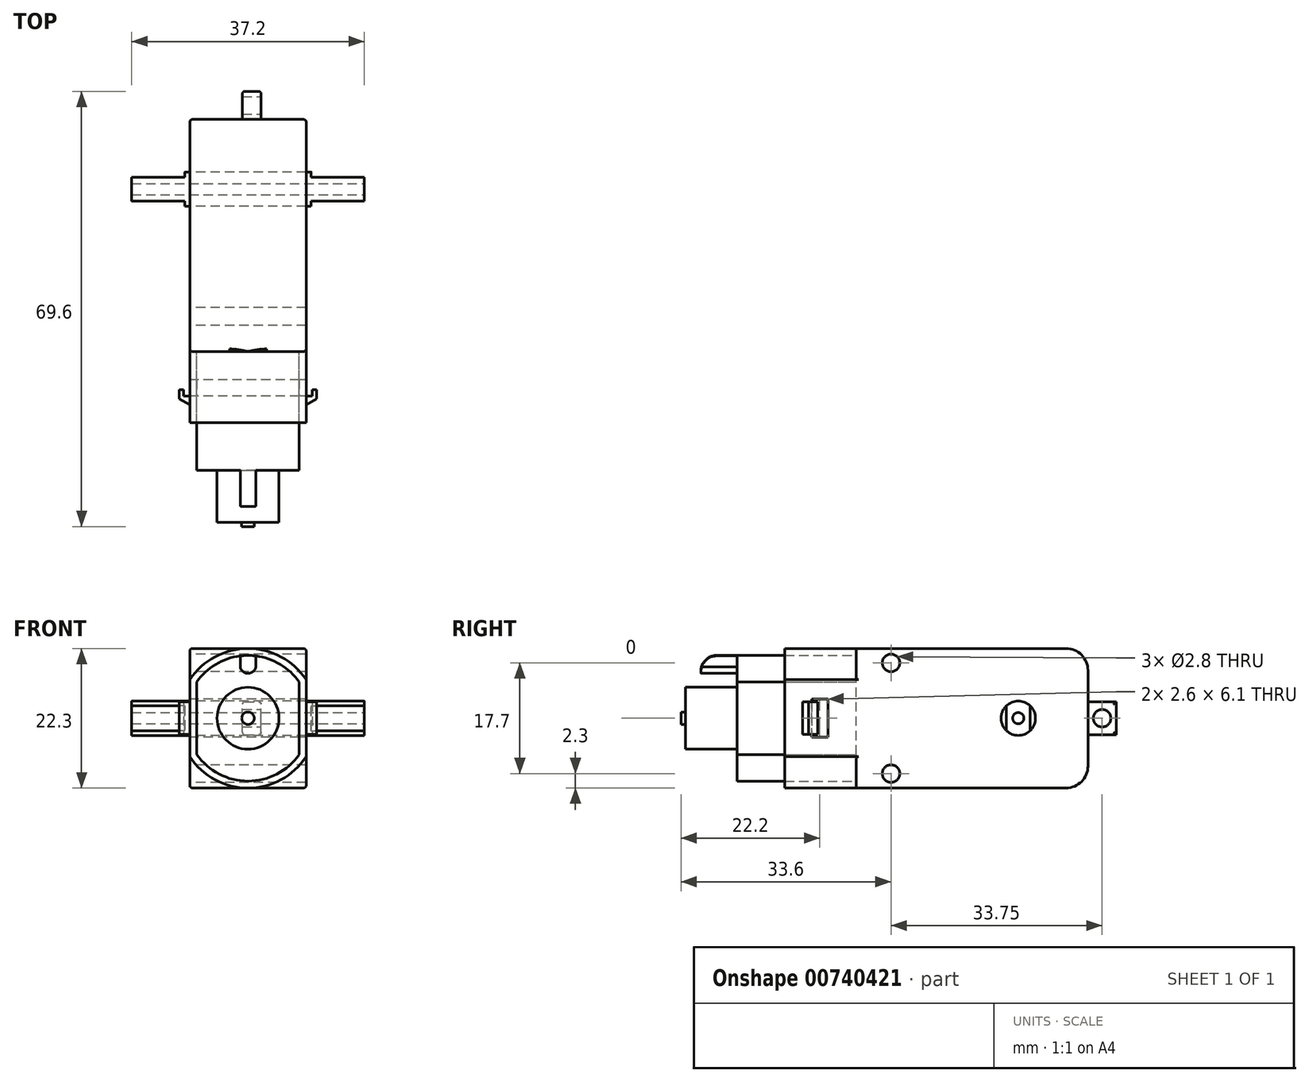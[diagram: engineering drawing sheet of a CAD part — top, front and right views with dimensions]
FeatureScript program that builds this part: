
annotation { "Feature Type Name" : "Feature", "Feature Type Description" : "" }
export const myFeature = defineFeature(function(context is Context, id is Id, definition is map)
    precondition{}
    {
        {
            var Q0;
            Q0=qCreatedBy(makeId("Front.planeOp"),FACE);
            var sketch = newSketch(context, id + "F0", { "sketchPlane" : qUnion([Q0])});
            skLineSegment(sketch, "E0.bottom", {"start": v(9.3, -11.15) * mm, "end": v(-9.3, -11.15) * mm});
            skLineSegment(sketch, "E0.top", {"start": v(9.3, 11.15) * mm, "end": v(-9.3, 11.15) * mm});
            skLineSegment(sketch, "E0.left", {"start": v(9.3, -11.15) * mm, "end": v(9.3, 11.15) * mm});
            skLineSegment(sketch, "E0.right", {"start": v(-9.3, -11.15) * mm, "end": v(-9.3, 11.15) * mm});
            skPoint(sketch, "E0.middle", {"position": v(0, 0) * mm});
            skSolve(sketch);
        }
        {
            var Q0;
            Q0=qSketchRegion(id+"F0",true);
            extrude(context, id + "F1", {"entities" : qUnion([Q0]), "depth" : 37.1 * mm});
        }
        {
            var Q0;
            Q0=makeQuery(id+"F1.opExtrude","SWEPT_FACE",FACE,{"disambiguationData":[OSD([sQuery(id+"F0.wireOp",EDGE,"E0.right")])]});
            var sketch = newSketch(context, id + "F2", { "sketchPlane" : qUnion([Q0])});
            skCircle(sketch, "E1", {"center": v(31.5, -8.85) * mm, "radius": 1.4 * mm});
            skLineSegment(sketch, "E2", {"start": v(0, 0) * mm, "end": v(37.1, 0) * mm, "construction": true});
            skCircle(sketch, "E3.MirrorC", {"center": v(31.5, 8.85) * mm, "radius": 1.4 * mm});
            skCircle(sketch, "E4", {"center": v(11.15, 0) * mm, "radius": 2.75 * mm});
            skSolve(sketch);
        }
        {
            var Q0;
            Q0=makeQuery(id+"F1.opExtrude","CAP_FACE",FACE,{"disambiguationData":[OSD([sQuery(id+"F0.wireOp",EDGE,"E0.bottom"),sQuery(id+"F0.wireOp",EDGE,"E0.top"),sQuery(id+"F0.wireOp",EDGE,"E0.left"),sQuery(id+"F0.wireOp",EDGE,"E0.right")])],"isStart":false});
            var sketch = newSketch(context, id + "F3", { "sketchPlane" : qUnion([Q0])});
            skArc(sketch, "E5", {"start": v(-9.3, -6.15) * mm, "mid": v(0, -11.15) * mm, "end": v(9.3, -6.15) * mm});
            skLineSegment(sketch, "E6.0", {"start": v(9.3, -6.15) * mm, "end": v(9.3, 6.15) * mm});
            skLineSegment(sketch, "E6.1", {"start": v(-9.3, -6.15) * mm, "end": v(-9.3, 6.15) * mm});
            skArc(sketch, "E7.trimOffspring", {"start": v(9.3, 6.15) * mm, "mid": v(0, 11.15) * mm, "end": v(-9.3, 6.15) * mm});
            skPoint(sketch, "E8.orphan", {"position": v(-9.3, 11.15) * mm});
            skPoint(sketch, "E9.orphan", {"position": v(9.3, 11.15) * mm});
            skPoint(sketch, "E10.orphan", {"position": v(9.3, -11.15) * mm});
            skPoint(sketch, "E11.orphan", {"position": v(-9.3, -11.15) * mm});
            skArc(sketch, "E12.0", {"start": v(8.2, 5.81) * mm, "mid": v(0, 10.05) * mm, "end": v(-8.2, 5.81) * mm});
            skLineSegment(sketch, "E12.1", {"start": v(8.2, -5.81) * mm, "end": v(8.2, 5.81) * mm});
            skArc(sketch, "E12.2", {"start": v(-8.2, -5.81) * mm, "mid": v(0, -10.05) * mm, "end": v(8.2, -5.81) * mm});
            skLineSegment(sketch, "E12.3", {"start": v(-8.2, -5.81) * mm, "end": v(-8.2, 5.81) * mm});
            skSolve(sketch);
        }
        {
            var Q0;
            Q0=qSketchRegion(id+"F3",true);
            extrude(context, id + "F4", {"entities" : qUnion([Q0]), "operationType" : NewBodyOperationType.ADD, "depth" : 11.4 * mm});
        }
        {
            var Q0;
            {var subQ0=sQuery(id+"F0.wireOp",EDGE,"F8vdl7xD-wS4J-gisc-z2d9-TpghqO1zXRkm");Q0=makeQuery(id+"F4.boolean.opBoolean","SPLIT",FACE,{"disambiguationData":[TD([makeQuery(id+"F1.opExtrude","SWEPT_FACE",FACE,{"disambiguationData":[OSD([subQ0])]}),makeQuery(id+"F4.opExtrude","SWEPT_FACE",FACE,{"disambiguationData":[OSD([sQuery(id+"F3.wireOp",EDGE,"E12.0")])]}),makeQuery(id+"F4.opExtrude","SWEPT_FACE",FACE,{"disambiguationData":[OSD([sQuery(id+"F3.wireOp",EDGE,"E12.1")])]}),makeQuery(id+"F4.opExtrude","SWEPT_FACE",FACE,{"disambiguationData":[OSD([sQuery(id+"F3.wireOp",EDGE,"E12.2")])]}),makeQuery(id+"F4.opExtrude","SWEPT_FACE",FACE,{"disambiguationData":[OSD([sQuery(id+"F3.wireOp",EDGE,"E12.3")])]})])],"derivedFrom":makeQuery(id+"F1.opExtrude","CAP_FACE",FACE,{"disambiguationData":[OSD([sQuery(id+"F0.wireOp",EDGE,"E0.bottom"),sQuery(id+"F0.wireOp",EDGE,"E0.top"),sQuery(id+"F0.wireOp",EDGE,"E0.left"),sQuery(id+"F0.wireOp",EDGE,"E0.right"),subQ0])],"isStart":false})});}
            var sketch = newSketch(context, id + "F5", { "sketchPlane" : qUnion([Q0])});
            skLineSegment(sketch, "E13.0", {"start": v(-8.2, -5.81) * mm, "end": v(-8.2, 5.81) * mm});
            skArc(sketch, "E13.1", {"start": v(8.2, 5.81) * mm, "mid": v(0, 10.05) * mm, "end": v(-8.2, 5.81) * mm});
            skLineSegment(sketch, "E13.2", {"start": v(8.2, -5.81) * mm, "end": v(8.2, 5.81) * mm});
            skArc(sketch, "E13.3", {"start": v(-8.2, -5.81) * mm, "mid": v(0, -10.05) * mm, "end": v(8.2, -5.81) * mm});
            skSolve(sketch);
        }
        {
            var Q0;
            Q0=qSketchRegion(id+"F5",true);
            extrude(context, id + "F6", {"entities" : qUnion([Q0]), "depth" : 24.8 * mm});
        }
        {
            var Q0;
            Q0=qSketchRegion(id+"F2",true);
            extrude(context, id + "F7", {"entities" : qUnion([Q0]), "operationType" : NewBodyOperationType.REMOVE, "oppositeDirection" : true, "depth" : 25 * mm});
        }
        {
            var Q0;
            Q0=qCreatedBy(makeId("Right.planeOp"),FACE);
            var sketch = newSketch(context, id + "F8", { "sketchPlane" : qUnion([Q0])});
            skCircle(sketch, "E14", {"center": v(-11.15, 0) * mm, "radius": 2.75 * mm});
            skSolve(sketch);
        }
        {
            var Q0;
            Q0=qSketchRegion(id+"F8",true);
            extrude(context, id + "F9", {"entities" : qUnion([Q0]), "endBound" : BoundingType.SYMMETRIC, "depth" : 37.2 * mm});
        }
        {
            var Q0;
            Q0=makeQuery(id+"F9.opExtrude","CAP_FACE",FACE,{"disambiguationData":[OSD([sQuery(id+"F8.wireOp",EDGE,"E14")])],"isStart":false});
            var sketch = newSketch(context, id + "F10", { "sketchPlane" : qUnion([Q0])});
            skLineSegment(sketch, "E15", {"start": v(-9.25, -1.99) * mm, "end": v(-9.25, 1.99) * mm});
            skLineSegment(sketch, "E16", {"start": v(-13.05, -1.99) * mm, "end": v(-13.05, 1.99) * mm});
            skPoint(sketch, "E17.start.orphan", {"position": v(-8.4, 0) * mm});
            skArc(sketch, "E18.0", {"start": v(-9.25, -1.99) * mm, "mid": v(-8.4, 0) * mm, "end": v(-9.25, 1.99) * mm});
            skArc(sketch, "E19.trimOffspring", {"start": v(-13.05, 1.99) * mm, "mid": v(-13.9, 0) * mm, "end": v(-13.05, -1.99) * mm});
            skSolve(sketch);
        }
        {
            var Q0;
            Q0=qSketchRegion(id+"F10",true);
            extrude(context, id + "F11", {"entities" : qUnion([Q0]), "operationType" : NewBodyOperationType.REMOVE, "oppositeDirection" : true, "depth" : 8.5 * mm});
        }
        {
            var Q0;
            Q0=makeQuery(id+"F9.opExtrude","CAP_FACE",FACE,{"disambiguationData":[OSD([sQuery(id+"F8.wireOp",EDGE,"E14")])],"isStart":true});
            var sketch = newSketch(context, id + "F12", { "sketchPlane" : qUnion([Q0])});
            skLineSegment(sketch, "E20", {"start": v(9.25, 1.99) * mm, "end": v(9.25, -1.99) * mm});
            skLineSegment(sketch, "E21", {"start": v(13.05, 1.99) * mm, "end": v(13.05, -1.99) * mm});
            skPoint(sketch, "E22.start.orphan", {"position": v(9.25, 0) * mm});
            skPoint(sketch, "E23.start.orphan", {"position": v(13.05, 0) * mm});
            skArc(sketch, "E24.0", {"start": v(9.25, 1.99) * mm, "mid": v(11.15, -2.75) * mm, "end": v(13.05, 1.99) * mm});
            skSolve(sketch);
        }
        {
            var Q0;
            Q0=qSketchRegion(id+"F12",true);
            extrude(context, id + "F13", {"entities" : qUnion([Q0]), "operationType" : NewBodyOperationType.REMOVE, "oppositeDirection" : true, "depth" : 8.5 * mm});
        }
        {
            var Q0;
            Q0=makeQuery(id+"F1.opExtrude","CAP_FACE",FACE,{"disambiguationData":[OSD([sQuery(id+"F0.wireOp",EDGE,"E0.bottom"),sQuery(id+"F0.wireOp",EDGE,"E0.top"),sQuery(id+"F0.wireOp",EDGE,"E0.left"),sQuery(id+"F0.wireOp",EDGE,"E0.right")])],"isStart":true});
            var sketch = newSketch(context, id + "F14", { "sketchPlane" : qUnion([Q0])});
            skPoint(sketch, "E25.middle", {"position": v(-0.6, 0) * mm});
            skLineSegment(sketch, "E26.bottom", {"start": v(0.9, -2.63) * mm, "end": v(-2.1, -2.63) * mm});
            skLineSegment(sketch, "E26.top", {"start": v(0.9, 2.63) * mm, "end": v(-2.1, 2.63) * mm});
            skLineSegment(sketch, "E26.left", {"start": v(0.9, -2.63) * mm, "end": v(0.9, 2.63) * mm});
            skLineSegment(sketch, "E26.right", {"start": v(-2.1, -2.63) * mm, "end": v(-2.1, 2.63) * mm});
            skSolve(sketch);
        }
        {
            var Q0;
            Q0=qSketchRegion(id+"F14",true);
            extrude(context, id + "F15", {"entities" : qUnion([Q0]), "operationType" : NewBodyOperationType.ADD, "depth" : 4.5 * mm});
        }
        {
            var Q0;
            Q0=makeQuery(id+"F4.boolean.opBoolean","MERGE",FACE,{"derivedFrom":[makeQuery(id+"F1.opExtrude","SWEPT_FACE",FACE,{"disambiguationData":[OSD([sQuery(id+"F0.wireOp",EDGE,"E0.right")])]}),makeQuery(id+"F4.opExtrude","SWEPT_FACE",FACE,{"disambiguationData":[OSD([sQuery(id+"F3.wireOp",EDGE,"E6.1")])]})]});
            var sketch = newSketch(context, id + "F16", { "sketchPlane" : qUnion([Q0])});
            skLineSegment(sketch, "E27.bottom", {"start": v(41.6, -3.05) * mm, "end": v(44.2, -3.05) * mm});
            skLineSegment(sketch, "E27.top", {"start": v(41.6, 3.05) * mm, "end": v(44.2, 3.05) * mm});
            skLineSegment(sketch, "E27.left", {"start": v(41.6, -3.05) * mm, "end": v(41.6, 3.05) * mm});
            skLineSegment(sketch, "E27.right", {"start": v(44.2, -3.05) * mm, "end": v(44.2, 3.05) * mm});
            skPoint(sketch, "E27.middle", {"position": v(42.9, 0) * mm});
            skSolve(sketch);
        }
        {
            var Q0;
            Q0=makeQuery(id+"F6.opExtrude","CAP_FACE",FACE,{"disambiguationData":[OSD([sQuery(id+"F5.wireOp",EDGE,"E13.0"),sQuery(id+"F5.wireOp",EDGE,"E13.1"),sQuery(id+"F5.wireOp",EDGE,"E13.2"),sQuery(id+"F5.wireOp",EDGE,"E13.3")])],"isStart":false});
            var sketch = newSketch(context, id + "F17", { "sketchPlane" : qUnion([Q0])});
            skCircle(sketch, "E28", {"center": v(0, 0) * mm, "radius": 4.95 * mm});
            skCircle(sketch, "E29", {"center": v(0, 0) * mm, "radius": 1 * mm});
            skSolve(sketch);
        }
        {
            var Q0;
            Q0=makeQuery(id+"F17.imprint","IMPRINT",FACE,{"disambiguationData":[TD([[makeQuery(id+"F17.imprint","IMPRINT",EDGE,{"derivedFrom":sQuery(id+"F17.wireOp",EDGE,"E29")}),1.0]])]});
            extrude(context, id + "F18", {"entities" : qUnion([Q0]), "operationType" : NewBodyOperationType.ADD, "depth" : 3.2 * mm});
        }
        {
            var Q0;
            Q0=makeQuery(id+"F17.imprint","IMPRINT",FACE,{"disambiguationData":[TD([[makeQuery(id+"F17.imprint","IMPRINT",EDGE,{"derivedFrom":sQuery(id+"F17.wireOp",EDGE,"E28")}),1.0]])]});
            extrude(context, id + "F19", {"entities" : qUnion([Q0]), "operationType" : NewBodyOperationType.ADD, "depth" : 2.5 * mm});
        }
        {
            var Q0;
            Q0=makeQuery(id+"F17.imprint","IMPRINT",FACE,{"disambiguationData":[TD([[makeQuery(id+"F17.imprint","IMPRINT",EDGE,{"derivedFrom":sQuery(id+"F17.wireOp",EDGE,"E28")}),-1.0]])]});
            var sketch = newSketch(context, id + "F20", { "sketchPlane" : qUnion([Q0])});
            skArc(sketch, "E30.0", {"start": v(-1.25, -9.97) * mm, "mid": v(0, -10.05) * mm, "end": v(1.25, -9.97) * mm});
            skLineSegment(sketch, "E31", {"start": v(-1.25, -9.97) * mm, "end": v(-1.25, -8.18) * mm});
            skLineSegment(sketch, "E32", {"start": v(1.25, -9.97) * mm, "end": v(1.25, -8.18) * mm});
            skArc(sketch, "E33", {"start": v(1.25, -8.18) * mm, "mid": v(0, -7.18) * mm, "end": v(-1.25, -8.18) * mm});
            skArc(sketch, "E34.MirrorCS", {"start": v(1.25, 8.18) * mm, "mid": v(0, 7.18) * mm, "end": v(-1.25, 8.18) * mm});
            skLineSegment(sketch, "E35.MirrorCS", {"start": v(1.25, 9.97) * mm, "end": v(1.25, 8.18) * mm});
            skLineSegment(sketch, "E36.MirrorCS", {"start": v(-1.25, 9.97) * mm, "end": v(-1.25, 8.18) * mm});
            skArc(sketch, "E37.0", {"start": v(1.25, 9.97) * mm, "mid": v(0, 10.05) * mm, "end": v(-1.25, 9.97) * mm});
            skPoint(sketch, "E38.orphan", {"position": v(-8.2, 5.81) * mm});
            skPoint(sketch, "E39.orphan", {"position": v(8.2, 5.81) * mm});
            skPoint(sketch, "E40.orphan", {"position": v(8.2, -5.81) * mm});
            skPoint(sketch, "E41.orphan", {"position": v(-8.2, -5.81) * mm});
            skSolve(sketch);
        }
        {
            var Q0;
            Q0=makeQuery(id+"F16.imprint","IMPRINT",FACE,{"disambiguationData":[TD([[makeQuery(id+"F16.imprint","IMPRINT",EDGE,{"derivedFrom":sQuery(id+"F16.wireOp",EDGE,"E27.bottom")}),1.0]])]});
            extrude(context, id + "F21", {"entities" : qUnion([Q0]), "operationType" : NewBodyOperationType.REMOVE, "oppositeDirection" : true, "depth" : 25 * mm});
        }
        {
            var Q0;
            Q0=qCreatedBy(makeId("Top.planeOp"),FACE);
            var sketch = newSketch(context, id + "F22", { "sketchPlane" : qUnion([Q0])});
            skPoint(sketch, "E42.0", {"position": v(-9.3, -44.2) * mm});
            skLineSegment(sketch, "E43", {"start": v(-9.3, -44.2) * mm, "end": v(-9.3, -45.65) * mm});
            skLineSegment(sketch, "E44", {"start": v(-9.3, -45.65) * mm, "end": v(-11, -44.7) * mm});
            skLineSegment(sketch, "E45", {"start": v(-11, -44.7) * mm, "end": v(-11, -43.2) * mm});
            skLineSegment(sketch, "E46", {"start": v(-11, -43.2) * mm, "end": v(-10.3, -43.2) * mm});
            skLineSegment(sketch, "E47", {"start": v(-10.3, -43.2) * mm, "end": v(-10.3, -44.2) * mm});
            skLineSegment(sketch, "E48", {"start": v(-10.3, -44.2) * mm, "end": v(-9.3, -44.2) * mm});
            skSolve(sketch);
        }
        {
            var Q0;
            Q0=makeQuery(id+"F22.imprint","IMPRINT",FACE,{"disambiguationData":[TD([[makeQuery(id+"F22.imprint","IMPRINT",EDGE,{"derivedFrom":sQuery(id+"F22.wireOp",EDGE,"E43")}),-1.0]])]});
            extrude(context, id + "F23", {"entities" : qUnion([Q0]), "operationType" : NewBodyOperationType.ADD, "endBound" : BoundingType.SYMMETRIC, "depth" : 5.2 * mm});
        }
        {
            var Q0;
            Q0=makeQuery(id+"F9.opExtrude","CAP_FACE",FACE,{"disambiguationData":[OSD([sQuery(id+"F8.wireOp",EDGE,"E14")])],"isStart":false});
            var sketch = newSketch(context, id + "F24", { "sketchPlane" : qUnion([Q0])});
            skCircle(sketch, "E49", {"center": v(-11.15, 0) * mm, "radius": 0.9 * mm});
            skSolve(sketch);
        }
        {
            var Q0;
            Q0=qSketchRegion(id+"F24",true);
            extrude(context, id + "F25", {"entities" : qUnion([Q0]), "operationType" : NewBodyOperationType.REMOVE, "endBound" : BoundingType.THROUGH_ALL, "oppositeDirection" : true, "depth" : 25 * mm});
        }
        {
            var Q0;
            Q0=qCreatedBy(makeId("Top.planeOp"),FACE);
            var sketch = newSketch(context, id + "F26", { "sketchPlane" : qUnion([Q0])});
            skPoint(sketch, "E50.0", {"position": v(9.3, -44.2) * mm});
            skLineSegment(sketch, "E51", {"start": v(9.3, -44.2) * mm, "end": v(9.3, -45.65) * mm});
            skLineSegment(sketch, "E52", {"start": v(9.3, -45.65) * mm, "end": v(11, -44.7) * mm});
            skLineSegment(sketch, "E53", {"start": v(11, -44.7) * mm, "end": v(11, -43.2) * mm});
            skLineSegment(sketch, "E54", {"start": v(11, -43.2) * mm, "end": v(10.3, -43.2) * mm});
            skLineSegment(sketch, "E55", {"start": v(10.3, -43.2) * mm, "end": v(10.3, -44.2) * mm});
            skLineSegment(sketch, "E56", {"start": v(10.3, -44.2) * mm, "end": v(9.3, -44.2) * mm});
            skSolve(sketch);
        }
        {
            var Q0;
            Q0=makeQuery(id+"F26.imprint","IMPRINT",FACE,{"disambiguationData":[TD([[makeQuery(id+"F26.imprint","IMPRINT",EDGE,{"derivedFrom":sQuery(id+"F26.wireOp",EDGE,"E51")}),1.0]])]});
            extrude(context, id + "F27", {"entities" : qUnion([Q0]), "operationType" : NewBodyOperationType.ADD, "endBound" : BoundingType.SYMMETRIC, "depth" : 5.2 * mm});
        }
        {
            var Q0;
            Q0=makeQuery(id+"F20.imprint","IMPRINT",FACE,{"disambiguationData":[TD([[makeQuery(id+"F20.imprint","IMPRINT",EDGE,{"derivedFrom":sQuery(id+"F20.wireOp",EDGE,"E34.MirrorCS")}),-1.0]])]});
            var Q1;
            Q1=makeQuery(id+"F20.imprint","IMPRINT",FACE,{"disambiguationData":[TD([[makeQuery(id+"F20.imprint","IMPRINT",EDGE,{"derivedFrom":sQuery(id+"F20.wireOp",EDGE,"E30.0")}),1.0]])]});
            extrude(context, id + "F28", {"entities" : qUnion([Q0, Q1]), "operationType" : NewBodyOperationType.REMOVE, "oppositeDirection" : true, "depth" : 5.8 * mm});
        }
        {
            var Q0;
            Q0=makeQuery(id+"F15.opExtrude","SWEPT_FACE",FACE,{"disambiguationData":[OSD([sQuery(id+"F14.wireOp",EDGE,"E26.right")])]});
            var sketch = newSketch(context, id + "F29", { "sketchPlane" : qUnion([Q0])});
            skPoint(sketch, "E57.end.orphan", {"position": v(-4.5, 0) * mm});
            skPoint(sketch, "E57.start.orphan", {"position": v(-3.65, 0) * mm});
            skPoint(sketch, "E58.start.orphan", {"position": v(-0.85, 0) * mm});
            skCircle(sketch, "E59", {"center": v(2.25, 0) * mm, "radius": 1.4 * mm});
            skLineSegment(sketch, "E60", {"start": v(2.25, 2.63) * mm, "end": v(2.25, 0) * mm, "construction": true});
            skLineSegment(sketch, "E61", {"start": v(4.5, 0) * mm, "end": v(2.25, 0) * mm, "construction": true});
            skSolve(sketch);
        }
        {
            var Q0;
            Q0=makeQuery(id+"F29.imprint","IMPRINT",FACE,{"disambiguationData":[TD([[makeQuery(id+"F29.imprint","IMPRINT",EDGE,{"derivedFrom":sQuery(id+"F29.wireOp",EDGE,"E59")}),1.0]])]});
            extrude(context, id + "F30", {"entities" : qUnion([Q0]), "operationType" : NewBodyOperationType.REMOVE, "endBound" : BoundingType.THROUGH_ALL, "oppositeDirection" : true, "depth" : 25 * mm, "offsetDistance" : 25 * mm});
        }
        {
            var Q0;
            Q0=makeQuery(id+"F1.opExtrude","CAP_EDGE",EDGE,{"disambiguationData":[OSD([sQuery(id+"F0.wireOp",EDGE,"E0.top")])],"isStart":true});
            var Q1;
            Q1=makeQuery(id+"F1.opExtrude","CAP_EDGE",EDGE,{"disambiguationData":[OSD([sQuery(id+"F0.wireOp",EDGE,"E0.bottom")])],"isStart":true});
            fillet(context, id + "F31", {"entities" : qUnion([Q0, Q1]), "radius" : 3.5 * mm, "tangentPropagation" : true, "allowEdgeOverflow" : false});
        }
        {
            var Q0;
            {var subQ0=sQuery(id+"F0.wireOp",EDGE,"E0.right");var subQ1=sQuery(id+"F0.wireOp",EDGE,"E0.top");Q0=makeQuery(id+"F4.boolean.opBoolean","SPLIT",EDGE,{"disambiguationData":[TD([makeQuery(id+"F1.opExtrude","SWEPT_FACE",FACE,{"disambiguationData":[OSD([subQ0])]})])],"derivedFrom":makeQuery(id+"F1.opExtrude","CAP_EDGE",EDGE,{"disambiguationData":[OSD([subQ1])],"isStart":false})});}
            var Q1;
            {var subQ0=sQuery(id+"F0.wireOp",EDGE,"E0.left");var subQ1=sQuery(id+"F0.wireOp",EDGE,"E0.top");Q1=makeQuery(id+"F4.boolean.opBoolean","SPLIT",EDGE,{"disambiguationData":[TD([makeQuery(id+"F1.opExtrude","SWEPT_FACE",FACE,{"disambiguationData":[OSD([subQ0])]})])],"derivedFrom":makeQuery(id+"F1.opExtrude","CAP_EDGE",EDGE,{"disambiguationData":[OSD([subQ1])],"isStart":false})});}
            var Q2;
            {var subQ0=sQuery(id+"F0.wireOp",EDGE,"E0.left");var subQ1=sQuery(id+"F0.wireOp",EDGE,"E0.bottom");Q2=makeQuery(id+"F4.boolean.opBoolean","SPLIT",EDGE,{"disambiguationData":[TD([makeQuery(id+"F1.opExtrude","SWEPT_FACE",FACE,{"disambiguationData":[OSD([subQ0])]})])],"derivedFrom":makeQuery(id+"F1.opExtrude","CAP_EDGE",EDGE,{"disambiguationData":[OSD([subQ1])],"isStart":false})});}
            var Q3;
            {var subQ0=sQuery(id+"F0.wireOp",EDGE,"E0.right");var subQ1=sQuery(id+"F0.wireOp",EDGE,"E0.bottom");Q3=makeQuery(id+"F4.boolean.opBoolean","SPLIT",EDGE,{"disambiguationData":[TD([makeQuery(id+"F1.opExtrude","SWEPT_FACE",FACE,{"disambiguationData":[OSD([subQ0])]})])],"derivedFrom":makeQuery(id+"F1.opExtrude","CAP_EDGE",EDGE,{"disambiguationData":[OSD([subQ1])],"isStart":false})});}
            var Q4;
            {var subQ0=sQuery(id+"F0.wireOp",EDGE,"E0.right");var subQ1=sQuery(id+"F0.wireOp",EDGE,"E0.bottom");Q4=makeQuery(id+"F4.boolean.opBoolean","SPLIT",EDGE,{"disambiguationData":[TD([makeQuery(id+"F1.opExtrude","SWEPT_FACE",FACE,{"disambiguationData":[OSD([subQ1])]})])],"derivedFrom":makeQuery(id+"F1.opExtrude","CAP_EDGE",EDGE,{"disambiguationData":[OSD([subQ0])],"isStart":false})});}
            var Q5;
            {var subQ0=sQuery(id+"F0.wireOp",EDGE,"E0.left");var subQ1=sQuery(id+"F0.wireOp",EDGE,"E0.bottom");Q5=makeQuery(id+"F4.boolean.opBoolean","SPLIT",EDGE,{"disambiguationData":[TD([makeQuery(id+"F1.opExtrude","SWEPT_FACE",FACE,{"disambiguationData":[OSD([subQ1])]})])],"derivedFrom":makeQuery(id+"F1.opExtrude","CAP_EDGE",EDGE,{"disambiguationData":[OSD([subQ0])],"isStart":false})});}
            var Q6;
            {var subQ0=sQuery(id+"F0.wireOp",EDGE,"E0.left");var subQ1=sQuery(id+"F0.wireOp",EDGE,"E0.top");Q6=makeQuery(id+"F4.boolean.opBoolean","SPLIT",EDGE,{"disambiguationData":[TD([makeQuery(id+"F1.opExtrude","SWEPT_FACE",FACE,{"disambiguationData":[OSD([subQ1])]})])],"derivedFrom":makeQuery(id+"F1.opExtrude","CAP_EDGE",EDGE,{"disambiguationData":[OSD([subQ0])],"isStart":false})});}
            var Q7;
            {var subQ0=sQuery(id+"F0.wireOp",EDGE,"E0.right");var subQ1=sQuery(id+"F0.wireOp",EDGE,"E0.top");Q7=makeQuery(id+"F4.boolean.opBoolean","SPLIT",EDGE,{"disambiguationData":[TD([makeQuery(id+"F1.opExtrude","SWEPT_FACE",FACE,{"disambiguationData":[OSD([subQ1])]})])],"derivedFrom":makeQuery(id+"F1.opExtrude","CAP_EDGE",EDGE,{"disambiguationData":[OSD([subQ0])],"isStart":false})});}
            var Q8;
            Q8=makeQuery(id+"F1.opExtrude","SWEPT_EDGE",EDGE,{"disambiguationData":[OSD([sQuery(id+"F0.wireOp",EDGE,"E0.top"),sQuery(id+"F0.wireOp",EDGE,"E0.right")])]});
            var Q9;
            Q9=makeQuery(id+"F1.opExtrude","SWEPT_EDGE",EDGE,{"disambiguationData":[OSD([sQuery(id+"F0.wireOp",EDGE,"E0.bottom"),sQuery(id+"F0.wireOp",EDGE,"E0.left")])]});
            var Q10;
            Q10=makeQuery(id+"F15.opExtrude","SWEPT_EDGE",EDGE,{"disambiguationData":[OSD([sQuery(id+"F14.wireOp",EDGE,"E26.top"),sQuery(id+"F14.wireOp",EDGE,"E26.right")])]});
            var Q11;
            Q11=makeQuery(id+"F15.opExtrude","CAP_EDGE",EDGE,{"disambiguationData":[OSD([sQuery(id+"F14.wireOp",EDGE,"E26.right")])],"isStart":false});
            var Q12;
            Q12=makeQuery(id+"F15.opExtrude","SWEPT_EDGE",EDGE,{"disambiguationData":[OSD([sQuery(id+"F14.wireOp",EDGE,"E26.bottom"),sQuery(id+"F14.wireOp",EDGE,"E26.right")])]});
            var Q13;
            Q13=makeQuery(id+"F15.opExtrude","SWEPT_EDGE",EDGE,{"disambiguationData":[OSD([sQuery(id+"F14.wireOp",EDGE,"E26.top"),sQuery(id+"F14.wireOp",EDGE,"E26.left")])]});
            var Q14;
            Q14=makeQuery(id+"F15.opExtrude","CAP_EDGE",EDGE,{"disambiguationData":[OSD([sQuery(id+"F14.wireOp",EDGE,"E26.left")])],"isStart":false});
            var Q15;
            Q15=makeQuery(id+"F15.opExtrude","SWEPT_EDGE",EDGE,{"disambiguationData":[OSD([sQuery(id+"F14.wireOp",EDGE,"E26.bottom"),sQuery(id+"F14.wireOp",EDGE,"E26.left")])]});
            fillet(context, id + "F32", {"entities" : qUnion([Q0, Q1, Q2, Q3, Q4, Q5, Q6, Q7, Q8, Q9, Q10, Q11, Q12, Q13, Q14, Q15]), "radius" : .4 * mm, "tangentPropagation" : true, "allowEdgeOverflow" : false});
        }
        {
            var Q0;
            {var subQ0=sQuery(id+"F5.wireOp",EDGE,"E13.0");var subQ1=sQuery(id+"F5.wireOp",EDGE,"E13.1");Q0=makeQuery(id+"F28.boolean.opBoolean","SPLIT",EDGE,{"disambiguationData":[TD([makeQuery(id+"F6.opExtrude","SWEPT_FACE",FACE,{"disambiguationData":[OSD([subQ0])]})])],"derivedFrom":makeQuery(id+"F6.opExtrude","CAP_EDGE",EDGE,{"disambiguationData":[OSD([subQ1])],"isStart":false})});}
            var Q1;
            {var subQ0=sQuery(id+"F5.wireOp",EDGE,"E13.0");var subQ1=sQuery(id+"F5.wireOp",EDGE,"E13.3");Q1=makeQuery(id+"F28.boolean.opBoolean","SPLIT",EDGE,{"disambiguationData":[TD([makeQuery(id+"F6.opExtrude","SWEPT_FACE",FACE,{"disambiguationData":[OSD([subQ0])]})])],"derivedFrom":makeQuery(id+"F6.opExtrude","CAP_EDGE",EDGE,{"disambiguationData":[OSD([subQ1])],"isStart":false})});}
            var Q2;
            {var subQ0=sQuery(id+"F5.wireOp",EDGE,"E13.3");var subQ1=sQuery(id+"F5.wireOp",EDGE,"E13.2");Q2=makeQuery(id+"F28.boolean.opBoolean","SPLIT",EDGE,{"disambiguationData":[TD([makeQuery(id+"F6.opExtrude","SWEPT_FACE",FACE,{"disambiguationData":[OSD([subQ1])]})])],"derivedFrom":makeQuery(id+"F6.opExtrude","CAP_EDGE",EDGE,{"disambiguationData":[OSD([subQ0])],"isStart":false})});}
            var Q3;
            {var subQ0=sQuery(id+"F5.wireOp",EDGE,"E13.2");var subQ1=sQuery(id+"F5.wireOp",EDGE,"E13.1");Q3=makeQuery(id+"F28.boolean.opBoolean","SPLIT",EDGE,{"disambiguationData":[TD([makeQuery(id+"F6.opExtrude","SWEPT_FACE",FACE,{"disambiguationData":[OSD([subQ0])]})])],"derivedFrom":makeQuery(id+"F6.opExtrude","CAP_EDGE",EDGE,{"disambiguationData":[OSD([subQ1])],"isStart":false})});}
            fillet(context, id + "F33", {"entities" : qUnion([Q0, Q1, Q2, Q3]), "radius" : 2.5 * mm, "tangentPropagation" : true, "allowEdgeOverflow" : false});
        }
    });
